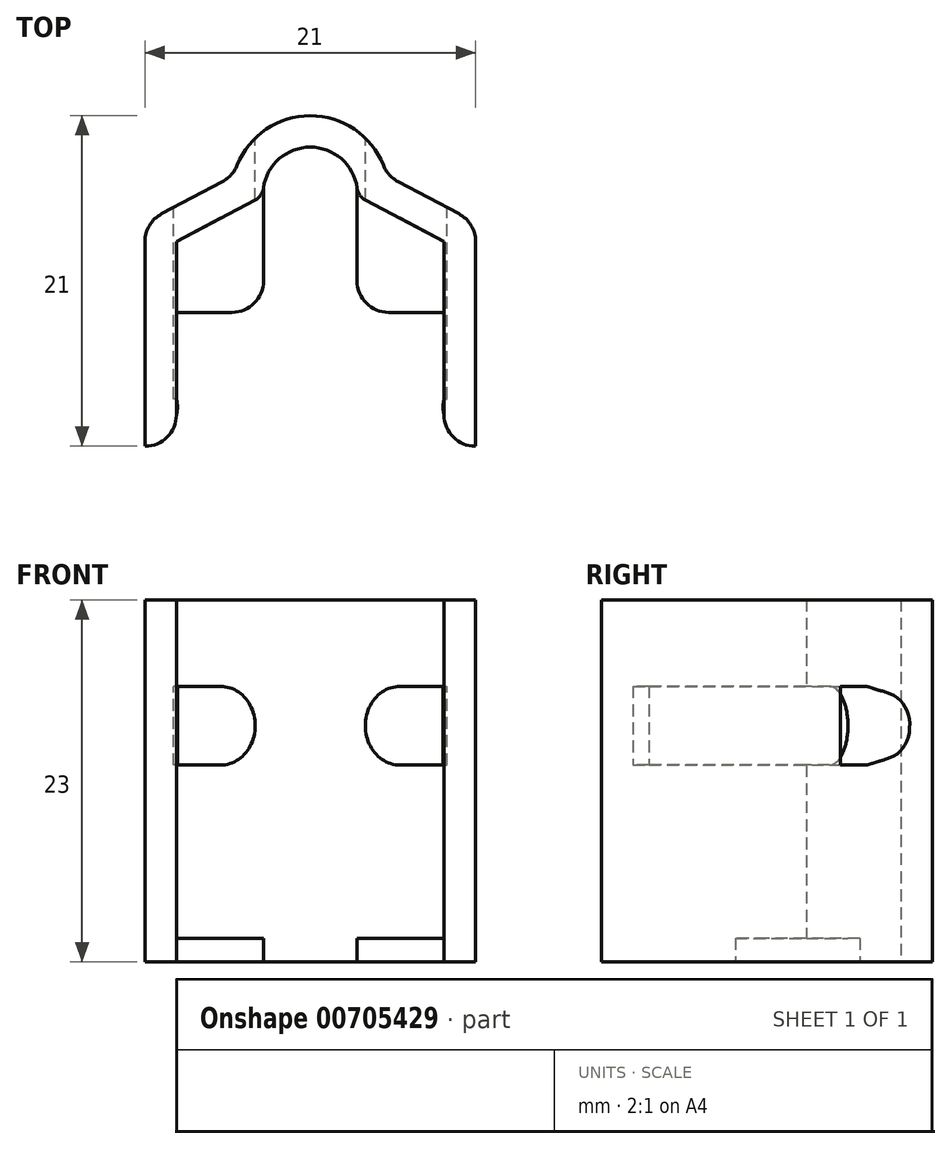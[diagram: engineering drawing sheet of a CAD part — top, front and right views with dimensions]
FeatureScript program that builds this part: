
annotation { "Feature Type Name" : "Feature", "Feature Type Description" : "" }
export const myFeature = defineFeature(function(context is Context, id is Id, definition is map)
    precondition{}
    {
        {
            var Q0;
            Q0=qCreatedBy(makeId("Top.planeOp"),FACE);
            var sketch = newSketch(context, id + "F0", { "sketchPlane" : qUnion([Q0])});
            skLineSegment(sketch, "E0", {"start": v(0, -17) * mm, "end": v(0, -6) * mm});
            skLineSegment(sketch, "E1", {"start": v(0, -6) * mm, "end": v(5, -3.35) * mm});
            skArc(sketch, "E2", {"start": v(8.5, 0) * mm, "mid": v(6.52, -0.74) * mm, "end": v(5.53, -2.6) * mm});
            skPoint(sketch, "E3.visualSharp", {"position": v(5.5, -3.09) * mm});
            skArc(sketch, "E3.filletArc", {"start": v(5, -3.35) * mm, "mid": v(5.36, -3.04) * mm, "end": v(5.53, -2.6) * mm});
            skArc(sketch, "E4.0", {"start": v(8.5, 2) * mm, "mid": v(5.7, 1.14) * mm, "end": v(3.85, -1.16) * mm});
            skLineSegment(sketch, "E5.0", {"start": v(-0.94, -4.23) * mm, "end": v(2.93, -2.19) * mm});
            skLineSegment(sketch, "E6.0", {"start": v(-2, -19) * mm, "end": v(-2, -6) * mm});
            skArc(sketch, "E7.filletArc", {"start": v(-0.94, -4.23) * mm, "mid": v(-1.71, -4.97) * mm, "end": v(-2, -6) * mm});
            skArc(sketch, "E8.filletArc", {"start": v(2.93, -2.19) * mm, "mid": v(3.48, -1.75) * mm, "end": v(3.85, -1.16) * mm});
            skLineSegment(sketch, "E9", {"start": v(-2, -19) * mm, "end": v(-2, -19) * mm});
            skPoint(sketch, "E10.visualSharp", {"position": v(0, -19) * mm});
            skArc(sketch, "E10.filletArc", {"start": v(-2, -19) * mm, "mid": v(-0.59, -18.41) * mm, "end": v(0, -17) * mm});
            skArc(sketch, "E11.MirrorCS", {"start": v(12, -3.35) * mm, "mid": v(11.64, -3.04) * mm, "end": v(11.47, -2.6) * mm});
            skArc(sketch, "E12.MirrorCS", {"start": v(17.94, -4.23) * mm, "mid": v(18.71, -4.97) * mm, "end": v(19, -6) * mm});
            skArc(sketch, "E13.MirrorCS", {"start": v(14.07, -2.19) * mm, "mid": v(13.52, -1.75) * mm, "end": v(13.15, -1.16) * mm});
            skArc(sketch, "E14.MirrorCS", {"start": v(19, -19) * mm, "mid": v(17.59, -18.41) * mm, "end": v(17, -17) * mm});
            skLineSegment(sketch, "E15.MirrorCS", {"start": v(17.94, -4.23) * mm, "end": v(14.07, -2.19) * mm});
            skLineSegment(sketch, "E16.MirrorCS", {"start": v(19, -19) * mm, "end": v(19, -6) * mm});
            skArc(sketch, "E17.MirrorCS", {"start": v(8.5, 2) * mm, "mid": v(11.3, 1.14) * mm, "end": v(13.15, -1.16) * mm});
            skLineSegment(sketch, "E18.MirrorCS", {"start": v(17, -6) * mm, "end": v(12, -3.35) * mm});
            skLineSegment(sketch, "E19.MirrorCS", {"start": v(17, -17) * mm, "end": v(17, -6) * mm});
            skPoint(sketch, "E20.MirrorP", {"position": v(11.5, -3.09) * mm});
            skPoint(sketch, "E21.MirrorP", {"position": v(17, -19) * mm});
            skArc(sketch, "E22.MirrorCS", {"start": v(8.5, 0) * mm, "mid": v(10.48, -0.74) * mm, "end": v(11.47, -2.6) * mm});
            skSolve(sketch);
        }
        {
            var Q0;
            Q0=makeQuery(id+"F0.imprint","IMPRINT",FACE,{"disambiguationData":[TD([[makeQuery(id+"F0.imprint","IMPRINT",EDGE,{"derivedFrom":sQuery(id+"F0.wireOp",EDGE,"E0")}),1.0]])]});
            extrude(context, id + "F1", {"entities" : qUnion([Q0]), "depth" : 23 * mm, "offsetDistance" : 25 * mm});
        }
        {
            var Q0;
            Q0=makeQuery(id+"F1.opExtrude","CAP_FACE",FACE,{"disambiguationData":[OSD([sQuery(id+"F0.wireOp",EDGE,"E0"),sQuery(id+"F0.wireOp",EDGE,"E1"),sQuery(id+"F0.wireOp",EDGE,"E2"),sQuery(id+"F0.wireOp",EDGE,"E3.filletArc"),sQuery(id+"F0.wireOp",EDGE,"E4.0"),sQuery(id+"F0.wireOp",EDGE,"E5.0"),sQuery(id+"F0.wireOp",EDGE,"E6.0"),sQuery(id+"F0.wireOp",EDGE,"E7.filletArc"),sQuery(id+"F0.wireOp",EDGE,"E8.filletArc"),sQuery(id+"F0.wireOp",EDGE,"E10.filletArc"),sQuery(id+"F0.wireOp",EDGE,"E11.MirrorCS"),sQuery(id+"F0.wireOp",EDGE,"E12.MirrorCS"),sQuery(id+"F0.wireOp",EDGE,"E13.MirrorCS"),sQuery(id+"F0.wireOp",EDGE,"E14.MirrorCS"),sQuery(id+"F0.wireOp",EDGE,"E15.MirrorCS"),sQuery(id+"F0.wireOp",EDGE,"E16.MirrorCS"),sQuery(id+"F0.wireOp",EDGE,"E17.MirrorCS"),sQuery(id+"F0.wireOp",EDGE,"E18.MirrorCS"),sQuery(id+"F0.wireOp",EDGE,"E19.MirrorCS"),sQuery(id+"F0.wireOp",EDGE,"E22.MirrorCS")])],"isStart":true});
            var sketch = newSketch(context, id + "F2", { "sketchPlane" : qUnion([Q0])});
            skLineSegment(sketch, "E23", {"start": v(0, 6) * mm, "end": v(0, 10.5) * mm});
            skLineSegment(sketch, "E24", {"start": v(0, 10.5) * mm, "end": v(3.53, 10.5) * mm});
            skLineSegment(sketch, "E25", {"start": v(5.53, 2.6) * mm, "end": v(5.53, 8.5) * mm});
            skPoint(sketch, "E26.orphan", {"position": v(6, 10.5) * mm});
            skPoint(sketch, "E27.visualSharp", {"position": v(5.53, 10.5) * mm});
            skArc(sketch, "E27.filletArc", {"start": v(5.53, 8.5) * mm, "mid": v(4.94, 9.91) * mm, "end": v(3.53, 10.5) * mm});
            skLineSegment(sketch, "E28.0", {"start": v(0, 6) * mm, "end": v(5, 3.35) * mm});
            skArc(sketch, "E29.0", {"start": v(5, 3.35) * mm, "mid": v(5.36, 3.04) * mm, "end": v(5.53, 2.6) * mm});
            skLineSegment(sketch, "E30", {"start": v(8.5, 0) * mm, "end": v(8.5, 12.38) * mm});
            skLineSegment(sketch, "E31.MirrorCS", {"start": v(11.47, 2.6) * mm, "end": v(11.47, 8.5) * mm});
            skLineSegment(sketch, "E32.MirrorCS", {"start": v(17, 6) * mm, "end": v(17, 10.5) * mm});
            skArc(sketch, "E33.MirrorCS", {"start": v(11.47, 8.5) * mm, "mid": v(12.06, 9.91) * mm, "end": v(13.47, 10.5) * mm});
            skLineSegment(sketch, "E34.MirrorCS", {"start": v(17, 6) * mm, "end": v(12, 3.35) * mm});
            skLineSegment(sketch, "E35.MirrorCS", {"start": v(17, 10.5) * mm, "end": v(13.47, 10.5) * mm});
            skPoint(sketch, "E36.MirrorP", {"position": v(11, 10.5) * mm});
            skPoint(sketch, "E37.MirrorP", {"position": v(11.47, 10.5) * mm});
            skArc(sketch, "E38.MirrorCS", {"start": v(12, 3.35) * mm, "mid": v(11.64, 3.04) * mm, "end": v(11.47, 2.6) * mm});
            skSolve(sketch);
        }
        {
            var Q0;
            Q0=makeQuery(id+"F2.imprint","IMPRINT",FACE,{"disambiguationData":[TD([[makeQuery(id+"F2.imprint","IMPRINT",EDGE,{"derivedFrom":sQuery(id+"F2.wireOp",EDGE,"E23")}),1.0]])]});
            var Q1;
            Q1=makeQuery(id+"F2.imprint","IMPRINT",FACE,{"disambiguationData":[TD([[makeQuery(id+"F2.imprint","IMPRINT",EDGE,{"derivedFrom":sQuery(id+"F2.wireOp",EDGE,"E31.MirrorCS")}),-1.0]])]});
            extrude(context, id + "F3", {"entities" : qUnion([Q0, Q1]), "operationType" : NewBodyOperationType.ADD, "oppositeDirection" : true, "depth" : 1.5 * mm, "offsetDistance" : 25 * mm});
        }
        {
            var Q0;
            Q0=makeQuery(id+"F1.opExtrude","SWEPT_FACE",FACE,{"disambiguationData":[OSD([sQuery(id+"F0.wireOp",EDGE,"E1")])]});
            var sketch = newSketch(context, id + "F4", { "sketchPlane" : qUnion([Q0])});
            skLineSegment(sketch, "E39", {"start": v(2.85, 23) * mm, "end": v(2.85, 17.5) * mm});
            skLineSegment(sketch, "E40", {"start": v(2.85, 17.5) * mm, "end": v(2.85, 12.5) * mm});
            skLineSegment(sketch, "E41", {"start": v(0.35, 12.5) * mm, "end": v(-2.8, 12.5) * mm});
            skLineSegment(sketch, "E42", {"start": v(0.35, 17.5) * mm, "end": v(-2.8, 17.5) * mm});
            skLineSegment(sketch, "E43", {"start": v(2.85, 15) * mm, "end": v(0.35, 15) * mm});
            skArc(sketch, "E44", {"start": v(0.35, 12.5) * mm, "mid": v(2.85, 15) * mm, "end": v(0.35, 17.5) * mm});
            skLineSegment(sketch, "E45", {"start": v(-2.8, 17.5) * mm, "end": v(-3, 17.5) * mm});
            skLineSegment(sketch, "E46", {"start": v(-2.8, 12.5) * mm, "end": v(-3, 12.5) * mm});
            skLineSegment(sketch, "E47", {"start": v(-3, 12.5) * mm, "end": v(-3, 17.5) * mm});
            skSolve(sketch);
        }
        {
            var Q0;
            Q0=qCreatedBy(makeId("Front.planeOp"),FACE);
            var sketch = newSketch(context, id + "F5", { "sketchPlane" : qUnion([Q0])});
            skLineSegment(sketch, "E48.0", {"start": v(-0.18, 12.5) * mm, "end": v(-0.18, 17.5) * mm});
            skLineSegment(sketch, "E49.0", {"start": v(0, 12.5) * mm, "end": v(-0.18, 12.5) * mm});
            skLineSegment(sketch, "E50.0", {"start": v(2.8, 12.5) * mm, "end": v(0, 12.5) * mm});
            skLineSegment(sketch, "E51.0", {"start": v(0, 17.5) * mm, "end": v(-0.18, 17.5) * mm});
            skLineSegment(sketch, "E52.0", {"start": v(2.8, 17.5) * mm, "end": v(0, 17.5) * mm});
            skEllipticalArc(sketch, "E53.0", {});
            const initialGuessF5  = {"E53.0": [0.002794049075847219, 0.015, 0, -1, 0.0025, 0.0022094697908676543, 0, 3.141592653589793]};
            skSetInitialGuess(sketch, initialGuessF5);
            skSolve(sketch);
        }
        {
            var Q0;
            Q0=makeQuery(id+"F5.imprint","IMPRINT",FACE,{"disambiguationData":[TD([[makeQuery(id+"F5.imprint","IMPRINT",EDGE,{"derivedFrom":sQuery(id+"F5.wireOp",EDGE,"E48.0")}),-1.0]])]});
            extrude(context, id + "F6", {"entities" : qUnion([Q0]), "depth" : 16 * mm, "offsetDistance" : 25 * mm, "hasSecondDirection" : true, "secondDirectionOppositeDirection" : true, "secondDirectionDepth" : 5 * mm});
        }
        {
            var Q0;
            Q0=qCreatedBy(makeId("Right.planeOp"),FACE);
            cPlane(context, id + "F7", {"entities" : qUnion([Q0]), "cplaneType" : CPlaneType.OFFSET, "offset" : 8.5 * mm, "width" : 150 * mm, "height" : 150 * mm});
        }
        {
            var Q0;
            Q0=makeQuery(id+"F6.opExtrude","SWEPT_BODY",BODY,{"disambiguationData":[OSD([sQuery(id+"F5.wireOp",EDGE,"E48.0"),sQuery(id+"F5.wireOp",EDGE,"E49.0"),sQuery(id+"F5.wireOp",EDGE,"E50.0"),sQuery(id+"F5.wireOp",EDGE,"E51.0"),sQuery(id+"F5.wireOp",EDGE,"E52.0"),sQuery(id+"F5.wireOp",EDGE,"E53.0")])]});
            var Q1;
            Q1=qCreatedBy(id+"F7.planeOp",FACE);
            mirror(context, id + "F8", {"entities" : qUnion([Q0]), "mirrorPlane" : qUnion([Q1])});
        }
        {
            var Q0;
            Q0=makeQuery(id+"F8.opPattern","COPY",BODY,{"derivedFrom":makeQuery(id+"F6.opExtrude","SWEPT_BODY",BODY,{"disambiguationData":[OSD([sQuery(id+"F5.wireOp",EDGE,"E48.0"),sQuery(id+"F5.wireOp",EDGE,"E49.0"),sQuery(id+"F5.wireOp",EDGE,"E50.0"),sQuery(id+"F5.wireOp",EDGE,"E51.0"),sQuery(id+"F5.wireOp",EDGE,"E52.0"),sQuery(id+"F5.wireOp",EDGE,"E53.0")])]}),"instanceName":"1"});
            var Q1;
            Q1=makeQuery(id+"F6.opExtrude","SWEPT_BODY",BODY,{"disambiguationData":[OSD([sQuery(id+"F5.wireOp",EDGE,"E48.0"),sQuery(id+"F5.wireOp",EDGE,"E49.0"),sQuery(id+"F5.wireOp",EDGE,"E50.0"),sQuery(id+"F5.wireOp",EDGE,"E51.0"),sQuery(id+"F5.wireOp",EDGE,"E52.0"),sQuery(id+"F5.wireOp",EDGE,"E53.0")])]});
            var Q2;
            Q2=makeQuery(id+"F1.opExtrude","SWEPT_BODY",BODY,{"disambiguationData":[OSD([sQuery(id+"F0.wireOp",EDGE,"E0"),sQuery(id+"F0.wireOp",EDGE,"E1"),sQuery(id+"F0.wireOp",EDGE,"E2"),sQuery(id+"F0.wireOp",EDGE,"E3.filletArc"),sQuery(id+"F0.wireOp",EDGE,"E4.0"),sQuery(id+"F0.wireOp",EDGE,"E5.0"),sQuery(id+"F0.wireOp",EDGE,"E6.0"),sQuery(id+"F0.wireOp",EDGE,"E7.filletArc"),sQuery(id+"F0.wireOp",EDGE,"E8.filletArc"),sQuery(id+"F0.wireOp",EDGE,"E10.filletArc"),sQuery(id+"F0.wireOp",EDGE,"E11.MirrorCS"),sQuery(id+"F0.wireOp",EDGE,"E12.MirrorCS"),sQuery(id+"F0.wireOp",EDGE,"E13.MirrorCS"),sQuery(id+"F0.wireOp",EDGE,"E14.MirrorCS"),sQuery(id+"F0.wireOp",EDGE,"E15.MirrorCS"),sQuery(id+"F0.wireOp",EDGE,"E16.MirrorCS"),sQuery(id+"F0.wireOp",EDGE,"E17.MirrorCS"),sQuery(id+"F0.wireOp",EDGE,"E18.MirrorCS"),sQuery(id+"F0.wireOp",EDGE,"E19.MirrorCS"),sQuery(id+"F0.wireOp",EDGE,"E22.MirrorCS")])]});
            booleanBodies(context, id + "F9", {"operationType" : BooleanOperationType.SUBTRACTION, "tools" : qUnion([Q0, Q1]), "targets" : qUnion([Q2])});
        }
        {
            var Q0;
            Q0=qCreatedBy(makeId("Top.planeOp"),FACE);
            cPlane(context, id + "F10", {"entities" : qUnion([Q0]), "cplaneType" : CPlaneType.OFFSET, "offset" : 12.5 * mm, "width" : 150 * mm, "height" : 150 * mm});
        }
        {
            var Q0;
            Q0=qCreatedBy(id+"F10.planeOp",FACE);
            var sketch = newSketch(context, id + "F11", { "sketchPlane" : qUnion([Q0])});
            skLineSegment(sketch, "E54", {"start": v(0, -16) * mm, "end": v(0, -17) * mm});
            skArc(sketch, "E55", {"start": v(0, -17) * mm, "mid": v(0.06, -16.5) * mm, "end": v(0, -16) * mm});
            skSolve(sketch);
        }
        {
            var Q0;
            Q0=makeQuery(id+"F11.imprint","IMPRINT",FACE,{"disambiguationData":[TD([[makeQuery(id+"F11.imprint","IMPRINT",EDGE,{"derivedFrom":sQuery(id+"F11.wireOp",EDGE,"E54")}),1.0]])]});
            extrude(context, id + "F12", {"entities" : qUnion([Q0]), "depth" : 5 * mm, "offsetDistance" : 25 * mm});
        }
        {
            var Q0;
            Q0=makeQuery(id+"F12.opExtrude","SWEPT_BODY",BODY,{"disambiguationData":[OSD([sQuery(id+"F11.wireOp",EDGE,"E54"),sQuery(id+"F11.wireOp",EDGE,"E55")])]});
            var Q1;
            Q1=qCreatedBy(id+"F7.planeOp",FACE);
            mirror(context, id + "F13", {"entities" : qUnion([Q0]), "mirrorPlane" : qUnion([Q1])});
        }
    });
